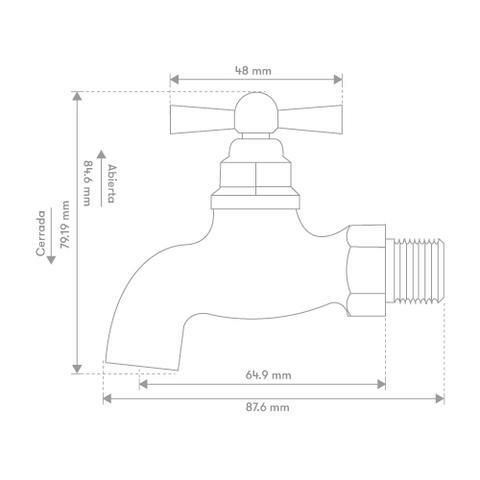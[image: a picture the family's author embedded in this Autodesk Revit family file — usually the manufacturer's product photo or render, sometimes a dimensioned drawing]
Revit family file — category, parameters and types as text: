
# Revit family: 01-9983-06 LLAVE MANGUERA LIVIANA METAL AMARILLA
name_source: partatom
category: Aparatos sanitarios
units: mm (PartAtom-declared; Revit-internal decimal feet)

## family parameters
Anfitrión = Cara
Compartido = No
Corte con vacíos al cargar = No
Cota de conector redondo = Diámetro de uso
Número OmniClass = 23.31.11.00
Punto de cálculo de habitación = No
Tipo de pieza = Normal

## types (1)
- 01-9983-06
    Acometida = Dim 1/2" NPT
    Alto = 46 mm  [stored 0.150919 ft]
    Ancho = 75 mm
    Ancho manija llave = 48 mm
    Conexión AC = Sí
    Conexión AF = Sí
    Conexión de residuos = No
    Conexión de ventilación = No
    Descripción = Llave jardin
    Elevación por defecto = 0 mm  [stored 0 ft]
    Fabricante = Gricol
    Imagen de tipo = LLAVE MANGUERA LIVIANA METAL AMARILLA.JPG
    Laton = Laton
    Link Ficha Tecnica = No encontrada en internet
    Metal - Zamak niquelado = Metal - Zamak niquelado
    Modelo = 01-9983-06
    Product Name = LLAVE MANGUERA LIVIANA METAL AMARILLA
    Salida = Dim 3/4" NH
    URL = https://www.gricol.com

note: [stored X ft] marks values corroborated as IEEE doubles in the binary element streams (Revit-internal decimal feet)

## geometry (parser evidence)
native form markers: Blend x2, Sweep x5
no freeform markers — native parametric forms only
